# Revit family: Haworth_Janus_Quinta_Sofas
name_source: partatom
category: Furniture
revit_build: Autodesk Revit 2018 (Build: 20170223_1515(x64)
units: mm (PartAtom-declared; Revit-internal decimal feet)

## family parameters
Always vertical = Yes
Cut with Voids When Loaded = No
OmniClass Number = 23.40.70.14.64.21
OmniClass Title = Systems Furniture
Room Calculation Point = No
Shared = No
Work Plane-Based = No

## types (2) — shared parameters
Actual Depth = 26"
Actual Height = 32"
Arm Height = 25"
Assembly Code = E2020200
Glide Finish = Haworth _ Polymer _ Black
Manufacturer = Haworth
Revision Number = 2
Seat Height = 16 1/2"
Size = Verify Final Dim. w/ Haworth
URL = http://www.haworth.com
URL - Product = https://www.haworth.com
Warranty = https://www.haworth.com
Wood Finish = Haworth _ Wood _ JanusQuinta _ Natural Teak JW1-97

## per-type parameters (varying)
| type | Actual Width | Description | Model | Three Seats | Two Seats |
| HCJC-QN-L3A-W - Three Seats | 74 3/4" | Haworth Janus Quinta - Three Seat Sofa | HCJC-QN-L3A-W | Yes | No |
| HCJC-QN-L2A-W - Two Seats | 53" | Haworth Janus Quinta - Two Seat Sofa | HCJC-QN-L2A-W | No | Yes |

## geometry (parser evidence)
native form markers: Sweep x2
no freeform markers — native parametric forms only
